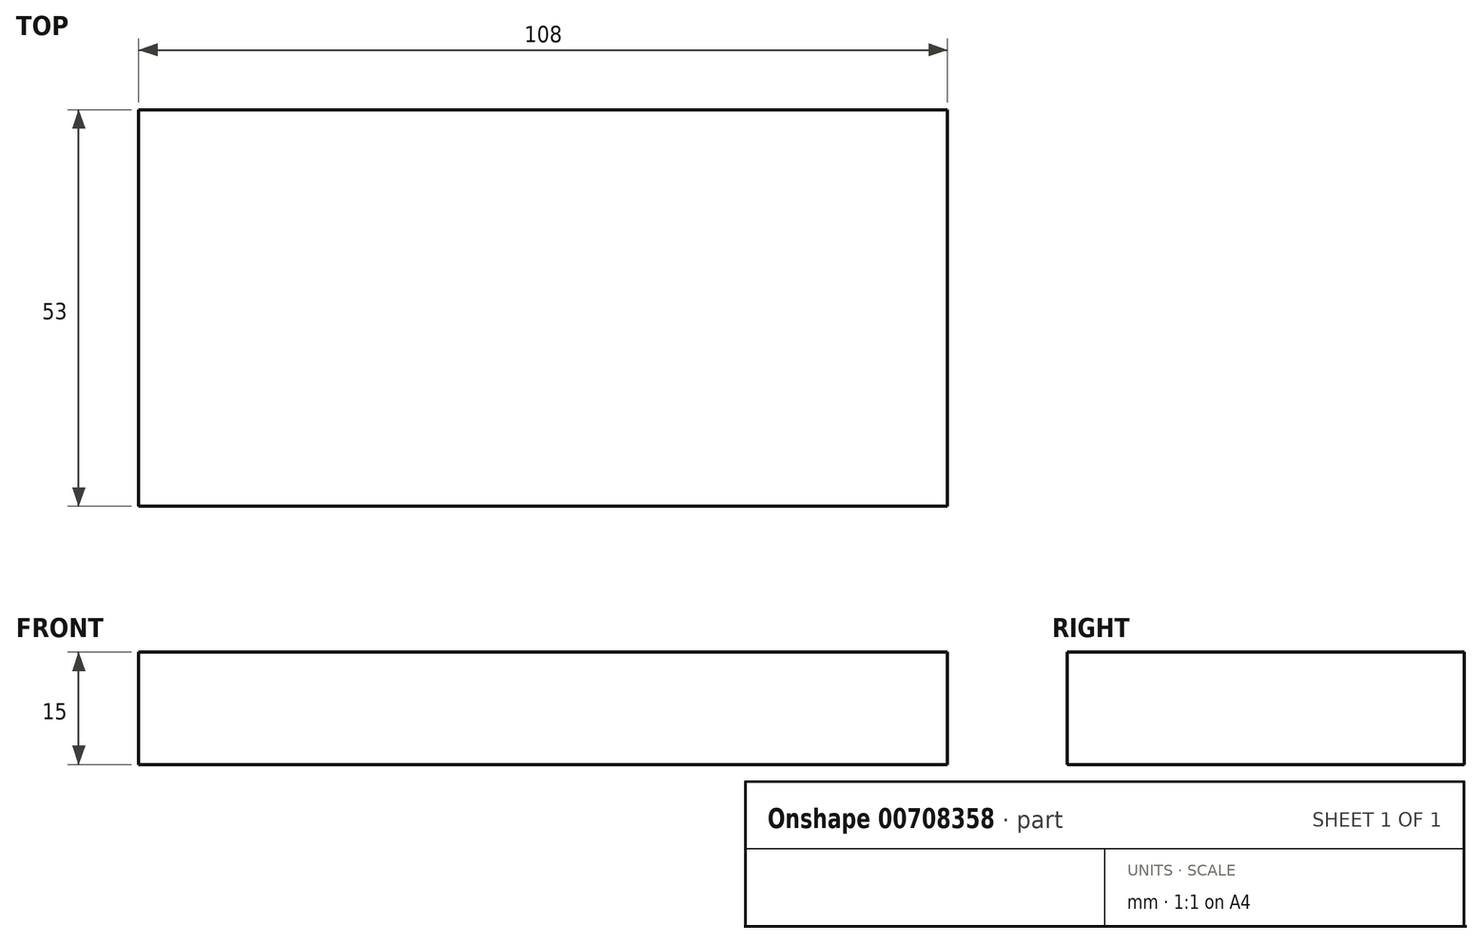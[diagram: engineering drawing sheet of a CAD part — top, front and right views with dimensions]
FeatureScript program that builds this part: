
annotation { "Feature Type Name" : "Feature", "Feature Type Description" : "" }
export const myFeature = defineFeature(function(context is Context, id is Id, definition is map)
    precondition{}
    {
        {
            var Q0;
            Q0=qCreatedBy(makeId("Top.planeOp"),FACE);
            var sketch = newSketch(context, id + "F0", { "sketchPlane" : qUnion([Q0])});
            skLineSegment(sketch, "E0.bottom", {"start": v(-108, -53) * mm, "end": v(0, -53) * mm});
            skLineSegment(sketch, "E0.top", {"start": v(-108, 0) * mm, "end": v(0, 0) * mm});
            skLineSegment(sketch, "E0.left", {"start": v(-108, -53) * mm, "end": v(-108, 0) * mm});
            skLineSegment(sketch, "E0.right", {"start": v(0, -53) * mm, "end": v(0, 0) * mm});
            skSolve(sketch);
        }
        {
            var Q0;
            Q0=makeQuery(id+"F0.imprint","IMPRINT",FACE,{"disambiguationData":[TD([[makeQuery(id+"F0.imprint","IMPRINT",EDGE,{"derivedFrom":sQuery(id+"F0.wireOp",EDGE,"E0.bottom")}),1.0]])]});
            extrude(context, id + "F1", {"entities" : qUnion([Q0]), "depth" : 15 * mm, "offsetDistance" : 25 * mm});
        }
    });
